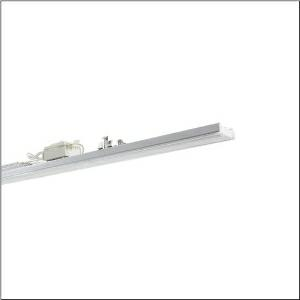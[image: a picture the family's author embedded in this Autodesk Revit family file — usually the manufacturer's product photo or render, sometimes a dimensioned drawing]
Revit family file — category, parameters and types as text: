
# Revit family: licross_r__11_recessed_mo_51tl18mn495g_f742
name_source: partatom
category: Lighting Fixtures
units: mm (PartAtom-declared; Revit-internal decimal feet)

## family parameters
Cut with Voids When Loaded = No
Host = Face
Light Source = No
Part Type = Normal
Room Calculation Point = No
Round Connector Dimension = Use Diameter
Shared = No

## types (1)
- --- (1 x LED, 9990 lm, 55.2 W, 4000K)
    Apparent Load = 55 VA
    CIE Flux Codes = 83 96 99 100 100
    Color Rendering = 80
    Color Temperature = 4000K
    Default Elevation = 1800 mm
    Description = Licross® 11 Recessed MO, luminaire insert, of sheet steel, coil coated, white, length: 1.500mm, width: 66mm, height: 67mm, LED rated luminous flux: 9.990lm, light colour: 840, control gear: ON/OFF Multilumen, with plug, 3-pole, with phase selection, mains connection: 220..240V, AC, 50/60Hz, rated input power: 55W, halogen-free wiring, primary light control with lens, of plastic, primary optical cover: cover, of PMMA, light emission: direct distribution, primary light characteristic: symmetric, protection rating (complete): IP40, insulation class (complete): insulation class I (protective earthing), certification: CE, ENEC, VDE, UKCA, protection symbol: D if used in an environment without relevant dust loads with corresponding accessories, impact resistance: IK06, permissible ambient temperature for indoor applications: -35..+40°C, corresponds to IFS (International Featured Standards) requirements for safety and quality in the food industry, reducing of maximum allowable ambient temperature of 5°C with ceiling mounting, packaging unit: 1 piece
    Height = 58 mm
    Lamp = 1 x LED
    Lamp Light Flux = 9990 lm
    Lamp Power = 55.2 W
    Lamp count = 1
    Length = 1500 mm
    Luminous efficacy = 181 lm/W
    Manufacturer = Siteco
    ModVariant = No
    Model = 51TL18MN495G
    Mounting Place = Ceiling
    Mounting Type = Pendant
    Number of Poles = 1
    OnlyDefault = Yes
    Power Factor = 1
    Product Name = Licross® 11 Recessed MO
    Product group = luminaire insert
    ProductGroupID = 902
    Protection Class = Protection class I
    Protection Degree = IP 40
    RLX_Detail_Level = 1
    RLX_Emergency_Light_Flux = 0 lm
    RLX_Emergency_Type = 0
    RLX_Emergency_Type_DB = No
    RlxData = <blob elided: 22113 chars, md5=0932ea7f>
    Socket = socket
    Standby Power = 0 W
    System Light Flux = 9990 lm
    System Power = 55 W
    Type Comments = factory setting: luminous flux: 100 % | (A | C | E) | 126 mA
    Type Image = l_1296930.jpg
    URL = http://relux.com
    VarID = @adj_084650
    Voltage = 0 V
    Weight = 0.00 kg
    Width = 66 mm

## geometry (parser evidence)
native form markers: Blend x4, Sweep x10
no freeform markers — native parametric forms only
